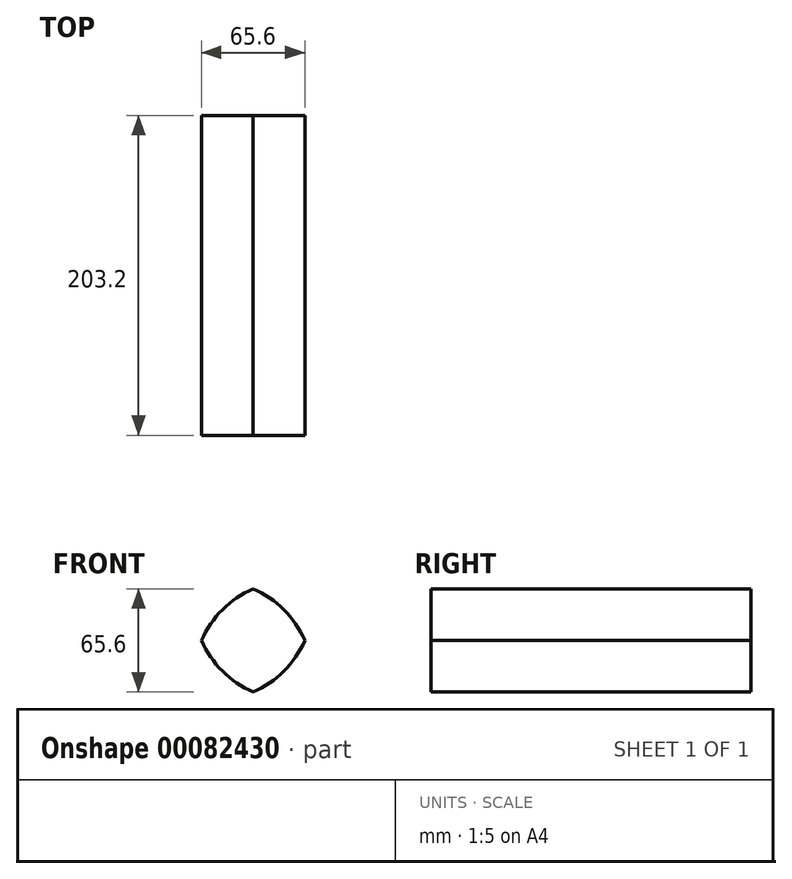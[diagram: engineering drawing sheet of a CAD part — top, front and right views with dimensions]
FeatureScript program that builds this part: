
annotation { "Feature Type Name" : "Feature", "Feature Type Description" : "" }
export const myFeature = defineFeature(function(context is Context, id is Id, definition is map)
    precondition{}
    {
        {
            var Q0;
            Q0=qCreatedBy(makeId("Right.planeOp"),FACE);
            var sketch = newSketch(context, id + "F0", { "sketchPlane" : qUnion([Q0])});
            skLineSegment(sketch, "E0.bottom", {"start": v(-101.6, 38.1) * mm, "end": v(101.6, 38.1) * mm});
            skLineSegment(sketch, "E0.top", {"start": v(-101.6, -38.1) * mm, "end": v(101.6, -38.1) * mm});
            skLineSegment(sketch, "E0.left", {"start": v(-101.6, 38.1) * mm, "end": v(-101.6, -38.1) * mm});
            skLineSegment(sketch, "E0.right", {"start": v(101.6, 38.1) * mm, "end": v(101.6, -38.1) * mm});
            skPoint(sketch, "E0.middle", {"position": v(0, 0) * mm});
            skSolve(sketch);
        }
        {
            var Q0;
            Q0 = qSketchRegion(id + "F0", true);
            extrude(context, id + "F1", {"entities" : qUnion([Q0]), "depth" : 76.2 * mm});
        }
        {
            var Q0;
            Q0=makeQuery(id+"F1.opExtrude","CAP_EDGE",EDGE,{"disambiguationData":[OSD([sQuery(id+"F0.wireOp",EDGE,"E0.bottom")])],"isStart":true});
            var Q1;
            Q1=makeQuery(id+"F1.opExtrude","CAP_EDGE",EDGE,{"disambiguationData":[OSD([sQuery(id+"F0.wireOp",EDGE,"E0.top")])],"isStart":true});
            var Q2;
            Q2=makeQuery(id+"F1.opExtrude","CAP_EDGE",EDGE,{"disambiguationData":[OSD([sQuery(id+"F0.wireOp",EDGE,"E0.bottom")])],"isStart":false});
            var Q3;
            Q3=makeQuery(id+"F1.opExtrude","CAP_EDGE",EDGE,{"disambiguationData":[OSD([sQuery(id+"F0.wireOp",EDGE,"E0.top")])],"isStart":false});
            fillet(context, id + "F2", {"entities" : qUnion([Q0, Q1, Q2, Q3]), "radius" : 63.5 * mm, "tangentPropagation" : true, "allowEdgeOverflow" : false});
        }
    });
